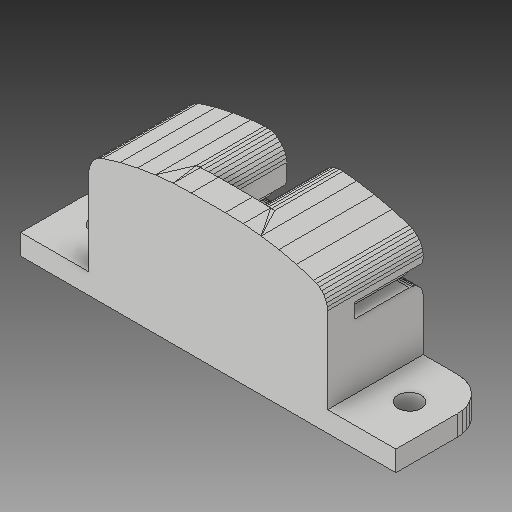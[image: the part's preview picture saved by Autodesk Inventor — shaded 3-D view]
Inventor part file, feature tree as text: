
AUTODESK INVENTOR PART (.ipt)
format: ipt  version: 2018 (Build 220112000, 112)  size: 401,920 bytes
history: native  units: mm
features: other x3, sketch x1
ambient origin geometry x8: Origin, YZ Plane, XZ Plane, XY Plane, X Axis, Y Axis, Z Axis, Center Point
bodies: Solid1 (feature_tree)
feature tree (4):
  other  "Y Belt Clamp.ipt"
  other  "Solid1::Y Belt Clamp.ipt"
  other  "TaggingFeature1"
  sketch  "Sketch2"  dims[d0=10.0mm]
